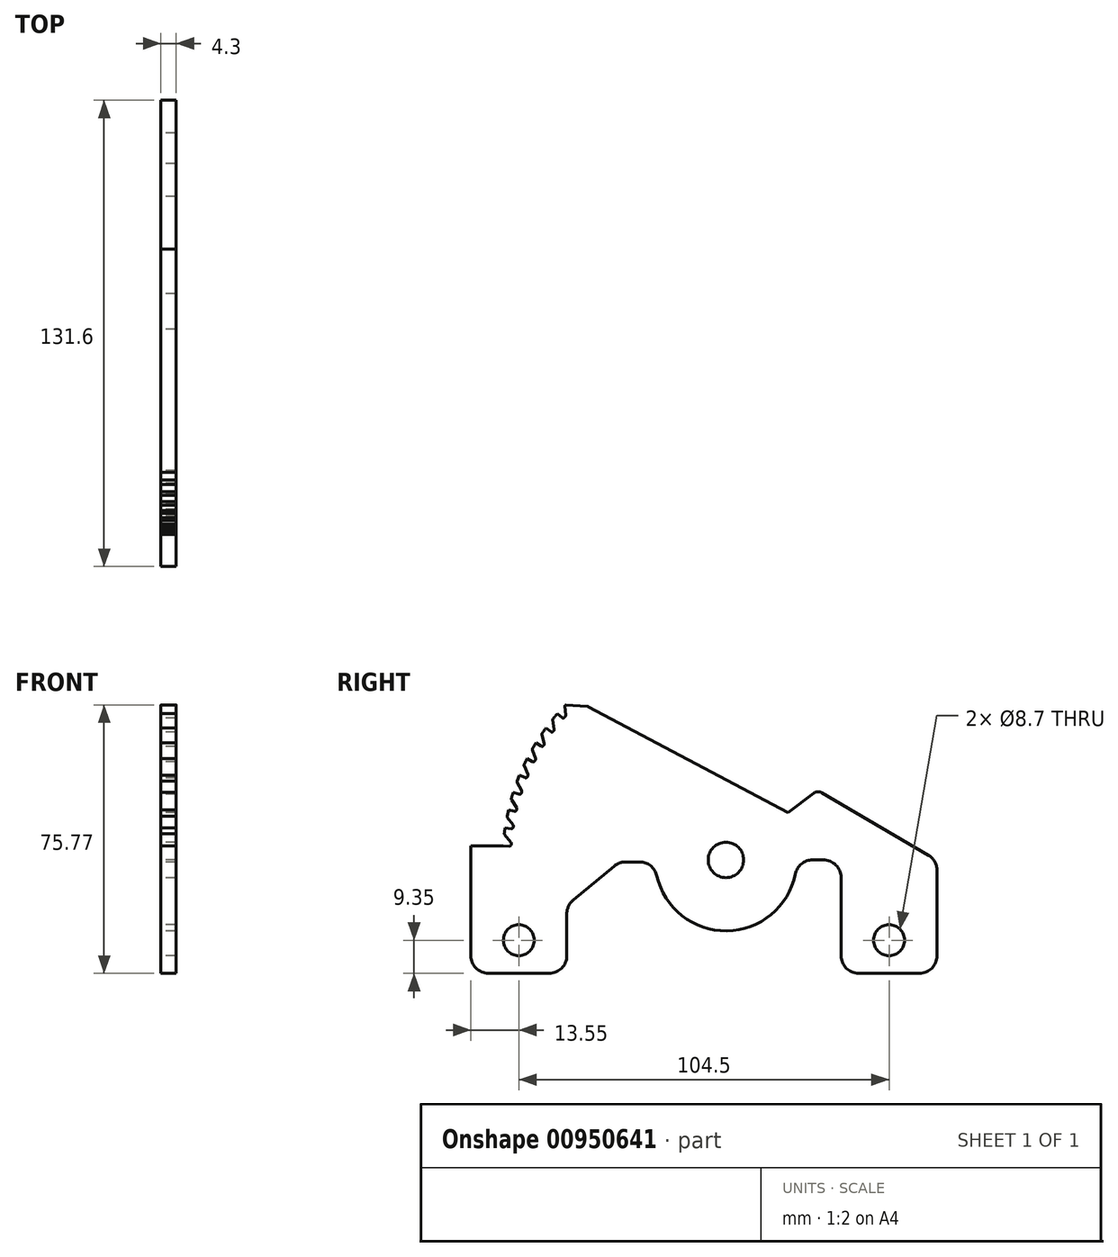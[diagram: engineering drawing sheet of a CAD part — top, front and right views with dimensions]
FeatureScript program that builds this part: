
annotation { "Feature Type Name" : "Feature", "Feature Type Description" : "" }
export const myFeature = defineFeature(function(context is Context, id is Id, definition is map)
    precondition{}
    {
        {
            var Q0;
            Q0=qCreatedBy(makeId("Right.planeOp"),FACE);
            var sketch = newSketch(context, id + "F0", { "sketchPlane" : qUnion([Q0])});
            skLineSegment(sketch, "E0.bottom", {"start": v(-5, 0) * mm, "end": v(-22.1, 0) * mm});
            skLineSegment(sketch, "E0.left", {"start": v(0, 5) * mm, "end": v(0, 29.04) * mm});
            skLineSegment(sketch, "E0.right", {"start": v(-131.6, 5) * mm, "end": v(-131.6, 36) * mm});
            skCircle(sketch, "E1", {"center": v(-118.05, 9.35) * mm, "radius": 4.35 * mm});
            skCircle(sketch, "E2.MirrorC", {"center": v(-13.55, 9.35) * mm, "radius": 4.35 * mm});
            skLineSegment(sketch, "E3", {"start": v(-59.6, 101.74) * mm, "end": v(-59.6, -6.98) * mm, "construction": true});
            skCircle(sketch, "E4", {"center": v(-59.6, 32) * mm, "radius": 5 * mm});
            skArc(sketch, "E5", {"start": v(-79.1, 27.56) * mm, "mid": v(-59.37, 12) * mm, "end": v(-40, 28.01) * mm});
            skLineSegment(sketch, "E6.MirrorCS", {"start": v(-104.5, 5) * mm, "end": v(-104.5, 16.84) * mm});
            skLineSegment(sketch, "E7", {"start": v(-13.55, 9.35) * mm, "end": v(-13.55, 67.35) * mm, "construction": true});
            skLineSegment(sketch, "E8.MirrorCS", {"start": v(-27.1, 5) * mm, "end": v(-27.1, 27.01) * mm});
            skLineSegment(sketch, "E9", {"start": v(-35.1, 32.01) * mm, "end": v(-32.1, 32.01) * mm});
            skLineSegment(sketch, "E10", {"start": v(-83.98, 31.45) * mm, "end": v(-87.9, 31.45) * mm});
            skLineSegment(sketch, "E11", {"start": v(-91.1, 30.3) * mm, "end": v(-102.7, 20.7) * mm});
            skPoint(sketch, "E12.orphan", {"position": v(-104.5, 93) * mm});
            skPoint(sketch, "E13.orphan", {"position": v(-27.1, 93) * mm});
            skLineSegment(sketch, "E14.trimOffspring", {"start": v(-109.5, 0) * mm, "end": v(-126.6, 0) * mm});
            skPoint(sketch, "E15.visualSharp", {"position": v(-27.1, 32.01) * mm});
            skArc(sketch, "E15.filletArc", {"start": v(-27.1, 27.01) * mm, "mid": v(-28.56, 30.55) * mm, "end": v(-32.1, 32.01) * mm});
            skPoint(sketch, "E16.visualSharp", {"position": v(-39.6, 32.01) * mm});
            skArc(sketch, "E16.filletArc", {"start": v(-35.1, 32.01) * mm, "mid": v(-38.27, 30.89) * mm, "end": v(-40, 28.01) * mm});
            skPoint(sketch, "E17.visualSharp", {"position": v(-79.6, 31.45) * mm});
            skArc(sketch, "E17.filletArc", {"start": v(-79.1, 27.56) * mm, "mid": v(-80.86, 30.36) * mm, "end": v(-83.98, 31.45) * mm});
            skPoint(sketch, "E18.visualSharp", {"position": v(-89.7, 31.45) * mm});
            skArc(sketch, "E18.filletArc", {"start": v(-87.9, 31.45) * mm, "mid": v(-89.6, 31.15) * mm, "end": v(-91.1, 30.3) * mm});
            skPoint(sketch, "E19.visualSharp", {"position": v(-104.5, 19.2) * mm});
            skArc(sketch, "E19.filletArc", {"start": v(-102.7, 20.7) * mm, "mid": v(-104.03, 18.97) * mm, "end": v(-104.5, 16.84) * mm});
            skPoint(sketch, "E20.visualSharp", {"position": v(-27.1, 0) * mm});
            skArc(sketch, "E20.filletArc", {"start": v(-27.1, 5) * mm, "mid": v(-25.64, 1.46) * mm, "end": v(-22.1, 0) * mm});
            skPoint(sketch, "E21.visualSharp", {"position": v(0, 0) * mm});
            skArc(sketch, "E21.filletArc", {"start": v(-5, 0) * mm, "mid": v(-1.46, 1.46) * mm, "end": v(0, 5) * mm});
            skPoint(sketch, "E22.visualSharp", {"position": v(-131.6, 0) * mm});
            skArc(sketch, "E22.filletArc", {"start": v(-131.6, 5) * mm, "mid": v(-130.14, 1.46) * mm, "end": v(-126.6, 0) * mm});
            skPoint(sketch, "E23.visualSharp", {"position": v(-104.5, 0) * mm});
            skArc(sketch, "E23.filletArc", {"start": v(-109.5, 0) * mm, "mid": v(-105.96, 1.46) * mm, "end": v(-104.5, 5) * mm});
            skLineSegment(sketch, "E24", {"start": v(-131.6, 36) * mm, "end": v(-122.47, 36) * mm});
            skPoint(sketch, "E25.orphan", {"position": v(-131.6, 93) * mm});
            skLineSegment(sketch, "E26", {"start": v(-103, 77.67) * mm, "end": v(-102.98, 77.66) * mm});
            skPoint(sketch, "E27.orphan", {"position": v(0, 93) * mm});
            skLineSegment(sketch, "E28", {"start": v(-32.57, 50.98) * mm, "end": v(-2.47, 33.35) * mm});
            skLineSegment(sketch, "E29.trimOffspring", {"start": v(-42.05, 45.33) * mm, "end": v(-34.8, 50.84) * mm});
            skPoint(sketch, "E30.visualSharp", {"position": v(0, 31.9) * mm});
            skArc(sketch, "E30.filletArc", {"start": v(0, 29.04) * mm, "mid": v(-0.66, 31.52) * mm, "end": v(-2.47, 33.35) * mm});
            skPoint(sketch, "E31.visualSharp", {"position": v(-33.73, 51.65) * mm});
            skArc(sketch, "E31.filletArc", {"start": v(-32.57, 50.98) * mm, "mid": v(-33.7, 51.25) * mm, "end": v(-34.8, 50.84) * mm});
            skLineSegment(sketch, "E32", {"start": v(-120.72, 35.89) * mm, "end": v(-122.47, 36) * mm, "construction": true});
            skLineSegment(sketch, "E33", {"start": v(-59.6, 32) * mm, "end": v(-103.65, 77.04) * mm, "construction": true});
            skArc(sketch, "E34.trimOffspring", {"start": v(-120.17, 36.65) * mm, "mid": v(-120.18, 36.5) * mm, "end": v(-120.2, 36.35) * mm});
            skLineSegment(sketch, "E35", {"start": v(-122.04, 39.15) * mm, "end": v(-120.28, 37.01) * mm});
            skLineSegment(sketch, "E36", {"start": v(-120.72, 35.89) * mm, "end": v(-122.47, 36) * mm});
            skLineSegment(sketch, "E37", {"start": v(-121.92, 41.1) * mm, "end": v(-121.94, 41.1) * mm});
            skLineSegment(sketch, "E38", {"start": v(-122, 41.1) * mm, "end": v(-119.52, 40.74) * mm});
            skPoint(sketch, "E39.visualSharp", {"position": v(-122.17, 39.31) * mm});
            skArc(sketch, "E39.filletArc", {"start": v(-122.15, 39.52) * mm, "mid": v(-122.13, 39.32) * mm, "end": v(-122.04, 39.15) * mm});
            skArc(sketch, "E40.filletArc", {"start": v(-120.17, 36.65) * mm, "mid": v(-120.2, 36.84) * mm, "end": v(-120.28, 37.01) * mm});
            skArc(sketch, "E41.filletArc", {"start": v(-120.72, 35.89) * mm, "mid": v(-120.36, 36.01) * mm, "end": v(-120.2, 36.35) * mm});
            skArc(sketch, "E42.trimOffspring", {"start": v(-121.94, 41.1) * mm, "mid": v(-122.05, 40.31) * mm, "end": v(-122.15, 39.52) * mm});
            skLineSegment(sketch, "E43.trimOffspring", {"start": v(-120.2, 40.84) * mm, "end": v(-121.94, 41.1) * mm, "construction": true});
            skArc(sketch, "E44.1.0", {"start": v(28.34, -122.4) * mm, "mid": v(28.19, -122.51) * mm, "end": v(28.1, -122.67) * mm});
            skArc(sketch, "E44.1.1", {"start": v(29.28, -122.5) * mm, "mid": v(29, -122.24) * mm, "end": v(28.62, -122.27) * mm});
            skArc(sketch, "E44.1.2", {"start": v(28.34, -122.4) * mm, "mid": v(28.48, -122.33) * mm, "end": v(28.62, -122.27) * mm});
            skLineSegment(sketch, "E44.1.3", {"start": v(24.55, -124.06) * mm, "end": v(25.38, -126.15) * mm, "construction": true});
            skArc(sketch, "E44.1.4", {"start": v(25.38, -126.15) * mm, "mid": v(26.11, -125.85) * mm, "end": v(26.85, -125.55) * mm});
            skPoint(sketch, "E44.1.5", {"position": v(27.04, -125.46) * mm});
            skLineSegment(sketch, "E44.1.6", {"start": v(27.12, -125.26) * mm, "end": v(28.1, -122.67) * mm});
            skLineSegment(sketch, "E44.1.7", {"start": v(29.28, -122.5) * mm, "end": v(30.06, -124.06) * mm, "construction": true});
            skArc(sketch, "E44.1.8", {"start": v(26.85, -125.55) * mm, "mid": v(27.01, -125.43) * mm, "end": v(27.12, -125.26) * mm});
            skLineSegment(sketch, "E44.1.9", {"start": v(29.28, -122.5) * mm, "end": v(30.06, -124.06) * mm});
            skArc(sketch, "E44.1.10", {"start": v(28.34, -122.4) * mm, "mid": v(28.48, -122.33) * mm, "end": v(28.62, -122.27) * mm});
            skLineSegment(sketch, "E44.1.11", {"start": v(25.37, -126.13) * mm, "end": v(25.38, -126.15) * mm});
            skArc(sketch, "E44.2.0", {"start": v(91.83, 85.74) * mm, "mid": v(92, 85.67) * mm, "end": v(92.2, 85.66) * mm});
            skArc(sketch, "E44.2.1", {"start": v(91.44, 86.6) * mm, "mid": v(91.37, 86.23) * mm, "end": v(91.58, 85.92) * mm});
            skArc(sketch, "E44.2.2", {"start": v(91.83, 85.74) * mm, "mid": v(91.7, 85.83) * mm, "end": v(91.58, 85.92) * mm});
            skLineSegment(sketch, "E44.2.3", {"start": v(95.16, 83.3) * mm, "end": v(96.56, 85.06) * mm, "construction": true});
            skArc(sketch, "E44.2.4", {"start": v(96.56, 85.05) * mm, "mid": v(95.93, 85.54) * mm, "end": v(95.3, 86.02) * mm});
            skPoint(sketch, "E44.2.5", {"position": v(95.13, 86.15) * mm});
            skLineSegment(sketch, "E44.2.6", {"start": v(94.92, 86.12) * mm, "end": v(92.2, 85.66) * mm});
            skLineSegment(sketch, "E44.2.7", {"start": v(91.44, 86.6) * mm, "end": v(92.41, 88.06) * mm, "construction": true});
            skArc(sketch, "E44.2.8", {"start": v(95.3, 86.02) * mm, "mid": v(95.12, 86.1) * mm, "end": v(94.92, 86.12) * mm});
            skLineSegment(sketch, "E44.2.9", {"start": v(91.44, 86.6) * mm, "end": v(92.41, 88.06) * mm});
            skArc(sketch, "E44.2.10", {"start": v(91.83, 85.74) * mm, "mid": v(91.7, 85.83) * mm, "end": v(91.58, 85.92) * mm});
            skLineSegment(sketch, "E44.2.11", {"start": v(96.55, 85.04) * mm, "end": v(96.56, 85.05) * mm});
            skLineSegment(sketch, "E45.MirrorCS", {"start": v(-114.2, 59.75) * mm, "end": v(-130.92, 68.24) * mm, "construction": true});
            skLineSegment(sketch, "E46.MirrorCS", {"start": v(-59.6, 32) * mm, "end": v(-105.02, 71.37) * mm, "construction": true});
            skLineSegment(sketch, "E47", {"start": v(-120.98, 46.13) * mm, "end": v(-119.29, 45.74) * mm});
            skPoint(sketch, "E48.visualSharp", {"position": v(-119.71, 40.77) * mm});
            skArc(sketch, "E48.filletArc", {"start": v(-120.2, 40.84) * mm, "mid": v(-119.84, 40.93) * mm, "end": v(-119.64, 41.26) * mm});
            skLineSegment(sketch, "E49", {"start": v(-121.26, 44) * mm, "end": v(-119.7, 41.93) * mm});
            skLineSegment(sketch, "E50", {"start": v(-119.6, 41.55) * mm, "end": v(-119.64, 41.26) * mm});
            skArc(sketch, "E51.trimOffspring", {"start": v(-121.92, 41.1) * mm, "mid": v(-122.04, 40.24) * mm, "end": v(-122.15, 39.4) * mm});
            skPoint(sketch, "E52.visualSharp", {"position": v(-121.4, 44.17) * mm});
            skArc(sketch, "E52.filletArc", {"start": v(-121.35, 44.4) * mm, "mid": v(-121.35, 44.18) * mm, "end": v(-121.26, 44) * mm});
            skArc(sketch, "E53.trimOffspring", {"start": v(-119.56, 41.76) * mm, "mid": v(-119.6, 41.5) * mm, "end": v(-119.64, 41.26) * mm});
            skPoint(sketch, "E54.visualSharp", {"position": v(-119.56, 41.76) * mm});
            skArc(sketch, "E54.filletArc", {"start": v(-119.6, 41.55) * mm, "mid": v(-119.6, 41.75) * mm, "end": v(-119.7, 41.93) * mm});
            skLineSegment(sketch, "E55", {"start": v(-120.08, 48.96) * mm, "end": v(-118.68, 46.78) * mm});
            skLineSegment(sketch, "E56", {"start": v(-119.63, 51.07) * mm, "end": v(-117.97, 50.54) * mm});
            skLineSegment(sketch, "E57", {"start": v(-118.62, 46.4) * mm, "end": v(-118.69, 46.1) * mm});
            skPoint(sketch, "E58.visualSharp", {"position": v(-118.8, 45.62) * mm});
            skArc(sketch, "E58.filletArc", {"start": v(-119.29, 45.74) * mm, "mid": v(-118.91, 45.8) * mm, "end": v(-118.69, 46.1) * mm});
            skPoint(sketch, "E59.visualSharp", {"position": v(-118.57, 46.6) * mm});
            skArc(sketch, "E59.filletArc", {"start": v(-118.62, 46.4) * mm, "mid": v(-118.61, 46.6) * mm, "end": v(-118.68, 46.78) * mm});
            skArc(sketch, "E60.filletArc", {"start": v(-120.14, 49.37) * mm, "mid": v(-120.16, 49.16) * mm, "end": v(-120.08, 48.96) * mm});
            skLineSegment(sketch, "E61", {"start": v(-120.98, 46.13) * mm, "end": v(-121.35, 44.4) * mm});
            skArc(sketch, "E62.filletArc", {"start": v(-117.97, 50.54) * mm, "mid": v(-117.6, 50.57) * mm, "end": v(-117.35, 50.86) * mm});
            skLineSegment(sketch, "E63", {"start": v(-118.5, 53.82) * mm, "end": v(-117.29, 51.53) * mm});
            skArc(sketch, "E64.trimOffspring", {"start": v(-117.26, 51.14) * mm, "mid": v(-117.3, 51) * mm, "end": v(-117.35, 50.86) * mm});
            skLineSegment(sketch, "E65", {"start": v(-117.88, 55.88) * mm, "end": v(-116.28, 55.22) * mm});
            skArc(sketch, "E66.trimOffspring", {"start": v(-119.63, 51.07) * mm, "mid": v(-119.9, 50.22) * mm, "end": v(-120.14, 49.37) * mm});
            skPoint(sketch, "E67.visualSharp", {"position": v(-118.6, 54.02) * mm});
            skArc(sketch, "E67.filletArc", {"start": v(-118.53, 54.23) * mm, "mid": v(-118.56, 54.02) * mm, "end": v(-118.5, 53.82) * mm});
            skPoint(sketch, "E68.visualSharp", {"position": v(-117.19, 51.34) * mm});
            skArc(sketch, "E68.filletArc", {"start": v(-117.26, 51.14) * mm, "mid": v(-117.23, 51.34) * mm, "end": v(-117.29, 51.53) * mm});
            skLineSegment(sketch, "E69", {"start": v(-116.54, 58.53) * mm, "end": v(-115.51, 56.15) * mm});
            skPoint(sketch, "E70.visualSharp", {"position": v(-115.81, 55.03) * mm});
            skArc(sketch, "E70.filletArc", {"start": v(-116.28, 55.22) * mm, "mid": v(-115.9, 55.22) * mm, "end": v(-115.62, 55.5) * mm});
            skLineSegment(sketch, "E71", {"start": v(-115.43, 55.95) * mm, "end": v(-115.39, 55.86) * mm});
            skArc(sketch, "E72.filletArc", {"start": v(-116.53, 58.94) * mm, "mid": v(-116.58, 58.74) * mm, "end": v(-116.54, 58.53) * mm});
            skLineSegment(sketch, "E73", {"start": v(-117.88, 55.88) * mm, "end": v(-118.53, 54.23) * mm});
            skLineSegment(sketch, "E74", {"start": v(-115.75, 60.54) * mm, "end": v(-114.2, 59.75) * mm});
            skArc(sketch, "E75.trimOffspring", {"start": v(-115.51, 55.76) * mm, "mid": v(-115.57, 55.62) * mm, "end": v(-115.62, 55.5) * mm});
            skPoint(sketch, "E76.visualSharp", {"position": v(-115.43, 55.95) * mm});
            skArc(sketch, "E76.filletArc", {"start": v(-115.51, 55.76) * mm, "mid": v(-115.47, 55.96) * mm, "end": v(-115.51, 56.15) * mm});
            skLineSegment(sketch, "E77", {"start": v(-113.24, 65) * mm, "end": v(-111.77, 64.1) * mm});
            skLineSegment(sketch, "E78.MirrorCS", {"start": v(-59.6, 32) * mm, "end": v(-108.25, 67.6) * mm, "construction": true});
            skLineSegment(sketch, "E79", {"start": v(-110.44, 69.2) * mm, "end": v(-109.02, 68.17) * mm});
            skLineSegment(sketch, "E80", {"start": v(-107.2, 73.25) * mm, "end": v(-105.88, 72.12) * mm});
            skLineSegment(sketch, "E81.trimOffspring", {"start": v(-98.45, 75.26) * mm, "end": v(-42.05, 45.33) * mm});
            skLineSegment(sketch, "E82.trimOffspring", {"start": v(-109.02, 68.17) * mm, "end": v(-110.44, 69.2) * mm, "construction": true});
            skLineSegment(sketch, "E83.trimOffspring", {"start": v(-105.88, 72.12) * mm, "end": v(-117.16, 81.9) * mm, "construction": true});
            skLineSegment(sketch, "E84", {"start": v(-114.2, 63.07) * mm, "end": v(-113.37, 60.61) * mm});
            skArc(sketch, "E85.trimOffspring", {"start": v(-115.75, 60.54) * mm, "mid": v(-116.14, 59.74) * mm, "end": v(-116.53, 58.94) * mm});
            skArc(sketch, "E86.trimOffspring", {"start": v(-113.4, 60.22) * mm, "mid": v(-113.46, 60.1) * mm, "end": v(-113.53, 59.96) * mm});
            skArc(sketch, "E87.filletArc", {"start": v(-114.2, 59.75) * mm, "mid": v(-113.82, 59.72) * mm, "end": v(-113.53, 59.96) * mm});
            skPoint(sketch, "E88.visualSharp", {"position": v(-113.3, 60.41) * mm});
            skArc(sketch, "E88.filletArc", {"start": v(-113.4, 60.22) * mm, "mid": v(-113.34, 60.42) * mm, "end": v(-113.37, 60.61) * mm});
            skPoint(sketch, "E89.visualSharp", {"position": v(-114.26, 63.28) * mm});
            skArc(sketch, "E89.filletArc", {"start": v(-114.15, 63.48) * mm, "mid": v(-114.22, 63.28) * mm, "end": v(-114.2, 63.07) * mm});
            skPoint(sketch, "E90.visualSharp", {"position": v(-111.34, 63.83) * mm});
            skArc(sketch, "E90.filletArc", {"start": v(-111.77, 64.1) * mm, "mid": v(-111.4, 64.03) * mm, "end": v(-111.08, 64.25) * mm});
            skLineSegment(sketch, "E91", {"start": v(-111.52, 67.34) * mm, "end": v(-110.87, 64.9) * mm});
            skArc(sketch, "E92.trimOffspring", {"start": v(-110.93, 64.5) * mm, "mid": v(-111, 64.37) * mm, "end": v(-111.08, 64.25) * mm});
            skArc(sketch, "E93.trimOffspring", {"start": v(-113.24, 65) * mm, "mid": v(-113.7, 64.24) * mm, "end": v(-114.15, 63.48) * mm});
            skPoint(sketch, "E94.visualSharp", {"position": v(-111.58, 67.57) * mm});
            skArc(sketch, "E94.filletArc", {"start": v(-111.45, 67.76) * mm, "mid": v(-111.53, 67.56) * mm, "end": v(-111.52, 67.34) * mm});
            skPoint(sketch, "E95.visualSharp", {"position": v(-110.81, 64.68) * mm});
            skArc(sketch, "E95.filletArc", {"start": v(-110.93, 64.5) * mm, "mid": v(-110.86, 64.69) * mm, "end": v(-110.87, 64.9) * mm});
            skPoint(sketch, "E96.visualSharp", {"position": v(-108.62, 67.88) * mm});
            skArc(sketch, "E96.filletArc", {"start": v(-109.02, 68.17) * mm, "mid": v(-108.65, 68.08) * mm, "end": v(-108.33, 68.28) * mm});
            skLineSegment(sketch, "E97", {"start": v(-108.44, 71.5) * mm, "end": v(-108.06, 68.89) * mm});
            skArc(sketch, "E98.trimOffspring", {"start": v(-108.15, 68.51) * mm, "mid": v(-108.24, 68.4) * mm, "end": v(-108.33, 68.28) * mm});
            skArc(sketch, "E99.trimOffspring", {"start": v(-110.42, 69.2) * mm, "mid": v(-110.94, 68.48) * mm, "end": v(-111.45, 67.76) * mm});
            skPoint(sketch, "E100.visualSharp", {"position": v(-108.48, 71.72) * mm});
            skArc(sketch, "E100.filletArc", {"start": v(-108.34, 71.9) * mm, "mid": v(-108.43, 71.71) * mm, "end": v(-108.44, 71.5) * mm});
            skPoint(sketch, "E101.visualSharp", {"position": v(-108.03, 68.68) * mm});
            skArc(sketch, "E101.filletArc", {"start": v(-108.15, 68.51) * mm, "mid": v(-108.07, 68.7) * mm, "end": v(-108.06, 68.89) * mm});
            skPoint(sketch, "E102.visualSharp", {"position": v(-105.5, 71.8) * mm});
            skArc(sketch, "E102.filletArc", {"start": v(-105.88, 72.12) * mm, "mid": v(-105.52, 72) * mm, "end": v(-105.18, 72.17) * mm});
            skLineSegment(sketch, "E103", {"start": v(-105.02, 75.4) * mm, "end": v(-104.86, 72.75) * mm});
            skArc(sketch, "E104.trimOffspring", {"start": v(-104.98, 72.39) * mm, "mid": v(-105.08, 72.28) * mm, "end": v(-105.18, 72.17) * mm});
            skArc(sketch, "E105.trimOffspring", {"start": v(-107.2, 73.25) * mm, "mid": v(-107.77, 72.58) * mm, "end": v(-108.34, 71.9) * mm});
            skPoint(sketch, "E106.visualSharp", {"position": v(-105.04, 75.62) * mm});
            skArc(sketch, "E106.filletArc", {"start": v(-104.9, 75.76) * mm, "mid": v(-105, 75.59) * mm, "end": v(-105.02, 75.4) * mm});
            skPoint(sketch, "E107.visualSharp", {"position": v(-104.84, 72.54) * mm});
            skArc(sketch, "E107.filletArc", {"start": v(-104.98, 72.39) * mm, "mid": v(-104.88, 72.56) * mm, "end": v(-104.86, 72.75) * mm});
            skLineSegment(sketch, "E108", {"start": v(-104.86, 75.77) * mm, "end": v(-98.65, 75.32) * mm});
            skPoint(sketch, "E109.visualSharp", {"position": v(-98.55, 75.31) * mm});
            skArc(sketch, "E109.filletArc", {"start": v(-98.45, 75.26) * mm, "mid": v(-98.55, 75.3) * mm, "end": v(-98.65, 75.32) * mm});
            skPoint(sketch, "E110.visualSharp", {"position": v(-104.88, 75.78) * mm});
            skArc(sketch, "E110.filletArc", {"start": v(-104.86, 75.77) * mm, "mid": v(-104.88, 75.77) * mm, "end": v(-104.9, 75.76) * mm});
            skSolve(sketch);
        }
        {
            var Q0;
            Q0=makeQuery(id+"F0.imprint","IMPRINT",FACE,{"disambiguationData":[TD([[makeQuery(id+"F0.imprint","IMPRINT",EDGE,{"derivedFrom":sQuery(id+"F0.wireOp",EDGE,"E0.bottom")}),-1.0]])]});
            extrude(context, id + "F1", {"entities" : qUnion([Q0]), "depth" : 4.3 * mm, "offsetDistance" : 25 * mm});
        }
    });
